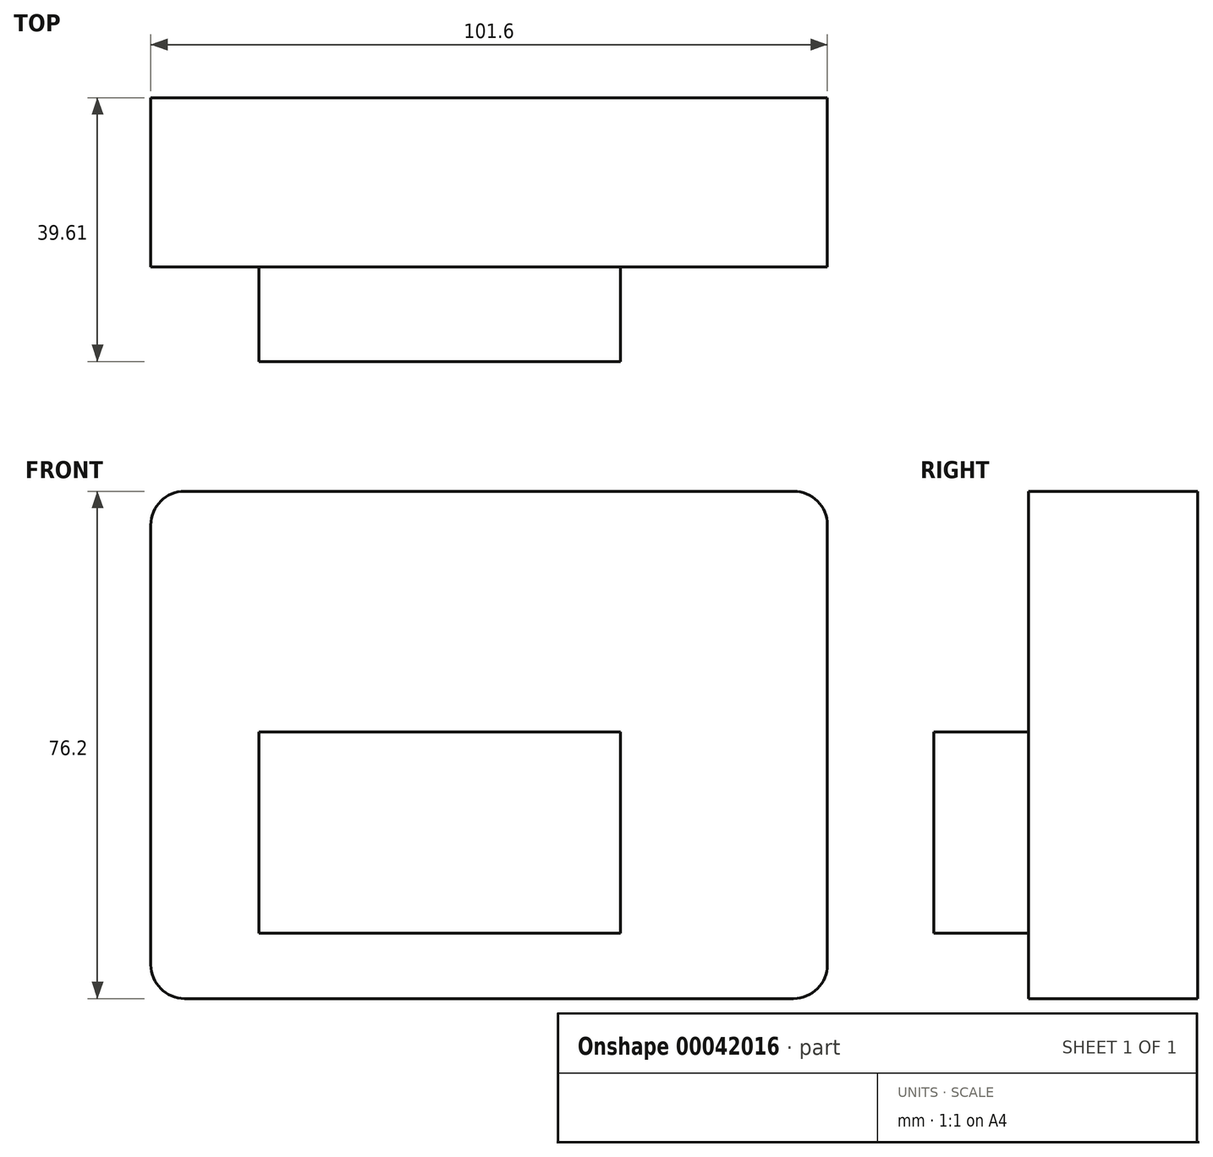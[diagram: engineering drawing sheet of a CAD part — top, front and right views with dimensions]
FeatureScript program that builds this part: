
annotation { "Feature Type Name" : "Feature", "Feature Type Description" : "" }
export const myFeature = defineFeature(function(context is Context, id is Id, definition is map)
    precondition{}
    {
        {
            var Q0;
            Q0=qCreatedBy(makeId("Front.planeOp"),FACE);
            var sketch = newSketch(context, id + "F0", { "sketchPlane" : qUnion([Q0])});
            skLineSegment(sketch, "E0.bottom", {"start": v(0, 0) * mm, "end": v(-101.6, 0) * mm});
            skLineSegment(sketch, "E0.top", {"start": v(0, 76.2) * mm, "end": v(-101.6, 76.2) * mm});
            skLineSegment(sketch, "E0.left", {"start": v(0, 0) * mm, "end": v(0, 76.2) * mm});
            skLineSegment(sketch, "E0.right", {"start": v(-101.6, 0) * mm, "end": v(-101.6, 76.2) * mm});
            skSolve(sketch);
        }
        {
            var Q0;
            Q0=makeQuery(id+"F0.imprint","IMPRINT",FACE,{"disambiguationData":[TD([[makeQuery(id+"F0.imprint","IMPRINT",EDGE,{"derivedFrom":sQuery(id+"F0.wireOp",EDGE,"E0.bottom")}),-1.0]])]});
            extrude(context, id + "F1", {"entities" : qUnion([Q0]), "depth" : 25.4 * mm});
        }
        {
            var Q0;
            Q0=makeQuery(id+"F1.opExtrude","CAP_FACE",FACE,{"disambiguationData":[OSD([sQuery(id+"F0.wireOp",EDGE,"E0.bottom"),sQuery(id+"F0.wireOp",EDGE,"E0.top"),sQuery(id+"F0.wireOp",EDGE,"E0.left"),sQuery(id+"F0.wireOp",EDGE,"E0.right")])],"isStart":false});
            var sketch = newSketch(context, id + "F2", { "sketchPlane" : qUnion([Q0])});
            skCircle(sketch, "E1", {"center": v(-81.85, 54.67) * mm, "radius": 5.58 * mm});
            skSolve(sketch);
        }
        {
            var Q0;
            Q0=sQuery(id+"F2.wireOp",EDGE,"E1");
            extrude(context, id + "F3", {"bodyType" : ToolBodyType.SURFACE, "surfaceEntities" : qUnion([Q0]), "depth" : 25.4 * mm});
        }
        {
            var Q0;
            Q0=makeQuery(id+"F1.opExtrude","SWEPT_EDGE",EDGE,{"disambiguationData":[OSD([sQuery(id+"F0.wireOp",EDGE,"E0.top"),sQuery(id+"F0.wireOp",EDGE,"E0.right")])]});
            var Q1;
            Q1=makeQuery(id+"F1.opExtrude","SWEPT_EDGE",EDGE,{"disambiguationData":[OSD([sQuery(id+"F0.wireOp",EDGE,"E0.top"),sQuery(id+"F0.wireOp",EDGE,"E0.left")])]});
            var Q2;
            Q2=makeQuery(id+"F1.opExtrude","SWEPT_EDGE",EDGE,{"disambiguationData":[OSD([sQuery(id+"F0.wireOp",EDGE,"E0.bottom"),sQuery(id+"F0.wireOp",EDGE,"E0.left")])]});
            var Q3;
            Q3=makeQuery(id+"F1.opExtrude","SWEPT_EDGE",EDGE,{"disambiguationData":[OSD([sQuery(id+"F0.wireOp",EDGE,"E0.bottom"),sQuery(id+"F0.wireOp",EDGE,"E0.right")])]});
            fillet(context, id + "F4", {"entities" : qUnion([Q0, Q1, Q2, Q3]), "radius" : 5.08 * mm, "tangentPropagation" : true, "allowEdgeOverflow" : false});
        }
        {
            var Q0;
            Q0=makeQuery(id+"F1.opExtrude","CAP_FACE",FACE,{"disambiguationData":[OSD([sQuery(id+"F0.wireOp",EDGE,"E0.bottom"),sQuery(id+"F0.wireOp",EDGE,"E0.top"),sQuery(id+"F0.wireOp",EDGE,"E0.left"),sQuery(id+"F0.wireOp",EDGE,"E0.right")])],"isStart":false});
            var sketch = newSketch(context, id + "F5", { "sketchPlane" : qUnion([Q0])});
            skLineSegment(sketch, "E2.bottom", {"start": v(-31.07, 40.05) * mm, "end": v(-85.39, 40.05) * mm});
            skLineSegment(sketch, "E2.top", {"start": v(-31.07, 9.84) * mm, "end": v(-85.39, 9.84) * mm});
            skLineSegment(sketch, "E2.left", {"start": v(-31.07, 40.05) * mm, "end": v(-31.07, 9.84) * mm});
            skLineSegment(sketch, "E2.right", {"start": v(-85.39, 40.05) * mm, "end": v(-85.39, 9.84) * mm});
            skSolve(sketch);
        }
        {
            var Q0;
            Q0=makeQuery(id+"F5.imprint","IMPRINT",FACE,{"disambiguationData":[TD([[makeQuery(id+"F5.imprint","IMPRINT",EDGE,{"derivedFrom":sQuery(id+"F5.wireOp",EDGE,"E2.bottom")}),1.0]])]});
            extrude(context, id + "F6", {"entities" : qUnion([Q0]), "operationType" : NewBodyOperationType.ADD, "depth" : 14.21 * mm});
        }
        {
            var Q0;
            Q0=makeQuery(id+"F3.opExtrude","SWEPT_BODY",BODY,{"disambiguationData":[OSD([sQuery(id+"F2.wireOp",EDGE,"E1")])]});
            deleteBodies(context, id + "F7", {"entities" : qUnion([Q0])});
        }
    });
